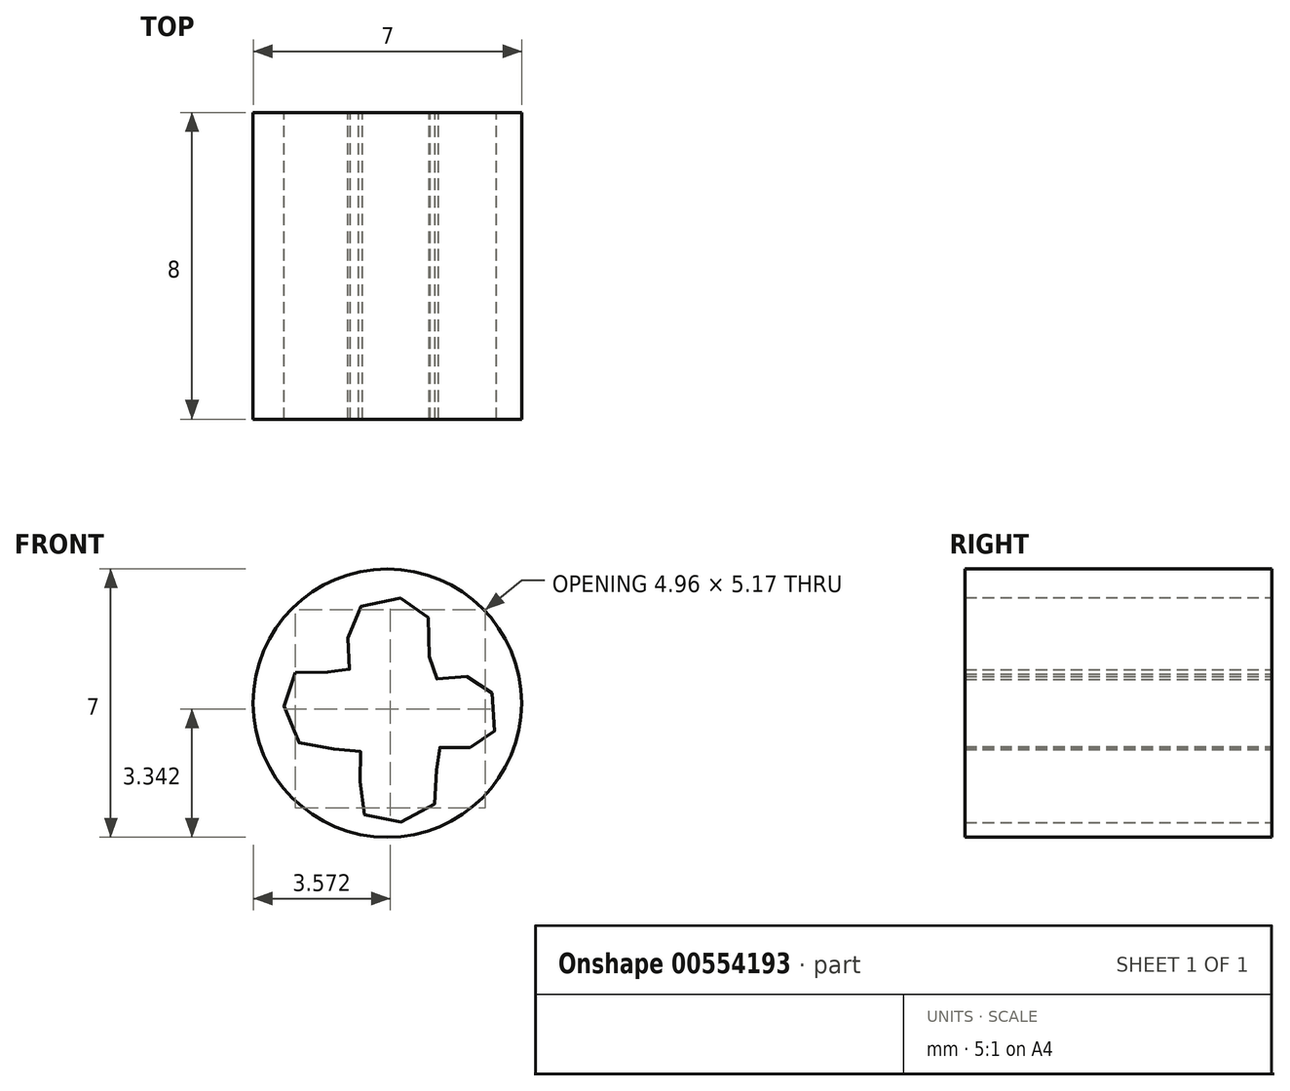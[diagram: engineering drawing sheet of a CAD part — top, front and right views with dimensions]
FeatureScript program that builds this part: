
annotation { "Feature Type Name" : "Feature", "Feature Type Description" : "" }
export const myFeature = defineFeature(function(context is Context, id is Id, definition is map)
    precondition{}
    {
        {
            var Q0;
            Q0=qCreatedBy(makeId("Front.planeOp"),FACE);
            var sketch = newSketch(context, id + "F0", { "sketchPlane" : qUnion([Q0])});
            skCircle(sketch, "E0", {"center": v(-8.63, 9.79) * mm, "radius": 3.5 * mm});
            skSolve(sketch);
        }
        {
            var Q0;
            Q0=makeQuery(id+"F0.imprint","IMPRINT",FACE,{"disambiguationData":[TD([[makeQuery(id+"F0.imprint","IMPRINT",EDGE,{"derivedFrom":sQuery(id+"F0.wireOp",EDGE,"E0")}),1.0]])]});
            extrude(context, id + "F1", {"entities" : qUnion([Q0]), "depth" : 8 * mm, "offsetDistance" : 25.4 * mm});
        }
        {
            var Q0;
            Q0=qCreatedBy(makeId("Front.planeOp"),FACE);
            var sketch = newSketch(context, id + "F2", { "sketchPlane" : qUnion([Q0])});
            skFitSpline(sketch, "E1", {"points": [v(-11.04, 10.58) * mm, v(-9.67, 10.58) * mm, v(-9.56, 12.06) * mm, v(-7.68, 12.23) * mm, v(-7.45, 10.47) * mm, v(-6.2, 10.4) * mm, v(-6.03, 8.76) * mm, v(-7.34, 8.59) * mm, v(-7.4, 7.16) * mm, v(-9.28, 6.94) * mm, v(-9.33, 8.53) * mm, v(-10.87, 8.7) * mm, v(-11.04, 10.58) * mm]});
            skSolve(sketch);
        }
        {
            var Q0;
            Q0=makeQuery(id+"F2.imprint","IMPRINT",FACE,{"disambiguationData":[TD([[makeQuery(id+"F2.imprint","IMPRINT",EDGE,{"derivedFrom":sQuery(id+"F2.wireOp",EDGE,"E1")}),-1.0]])]});
            extrude(context, id + "F3", {"entities" : qUnion([Q0]), "operationType" : NewBodyOperationType.REMOVE, "depth" : 8.38 * mm, "offsetDistance" : 25.4 * mm});
        }
    });
